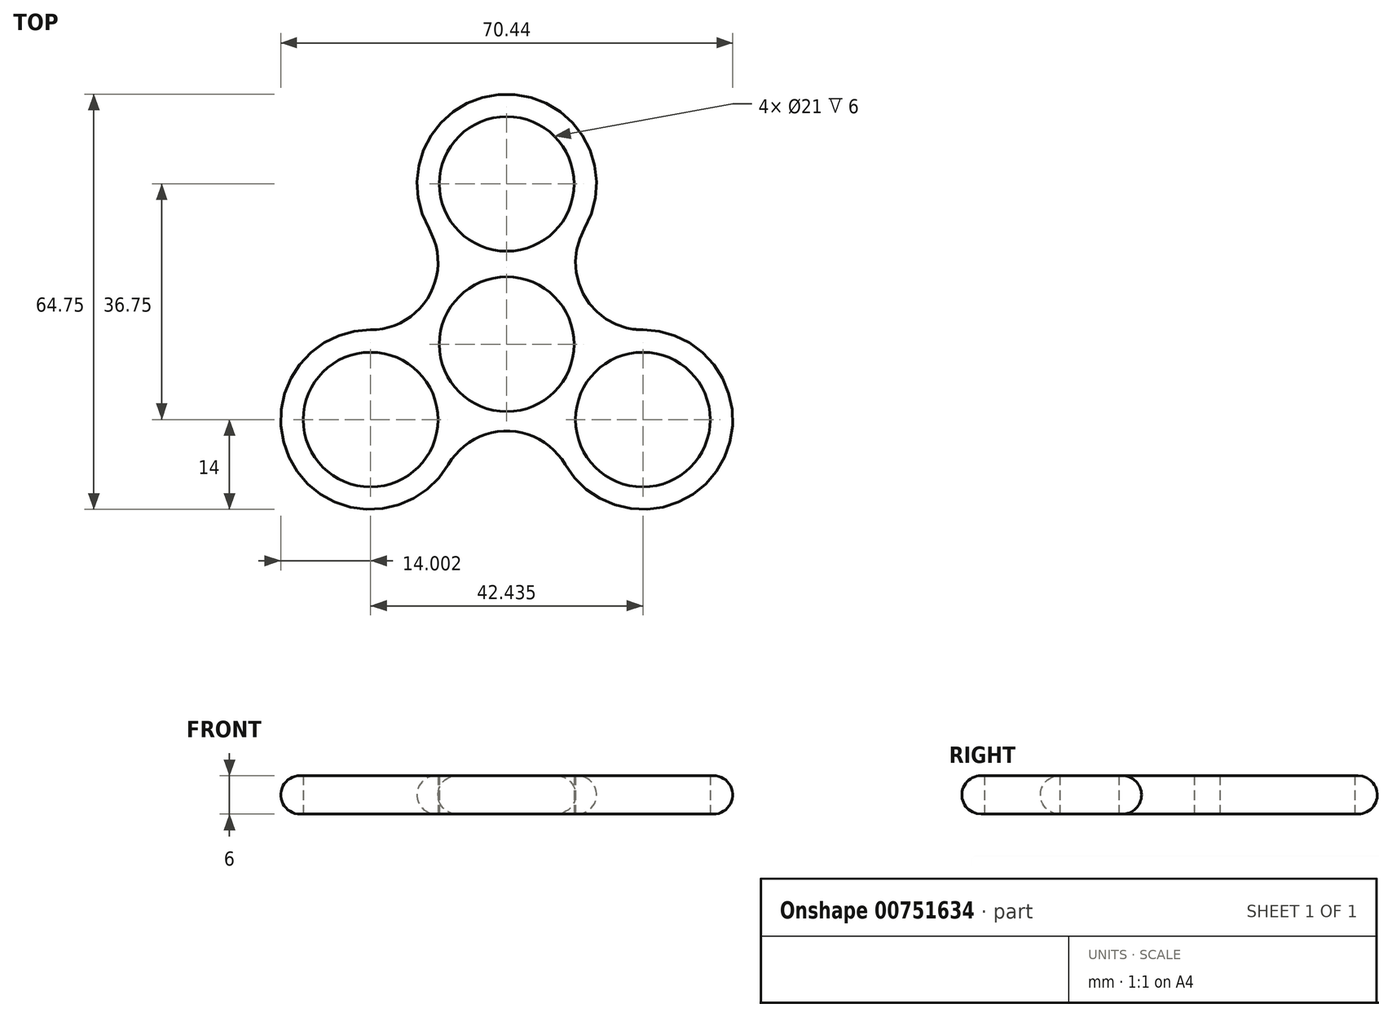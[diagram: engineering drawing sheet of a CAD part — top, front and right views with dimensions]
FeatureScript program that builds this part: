
annotation { "Feature Type Name" : "Feature", "Feature Type Description" : "" }
export const myFeature = defineFeature(function(context is Context, id is Id, definition is map)
    precondition{}
    {
        {
            var Q0;
            Q0=qCreatedBy(makeId("Top.planeOp"),FACE);
            var sketch = newSketch(context, id + "F0", { "sketchPlane" : qUnion([Q0])});
            skCircle(sketch, "E0", {"center": v(0, 0) * mm, "radius": 10.5 * mm});
            skCircle(sketch, "E1", {"center": v(0, 25) * mm, "radius": 10.5 * mm});
            skArc(sketch, "E2.1.0", {"start": v(-21.22, 2.25) * mm, "mid": v(-12.12, 7.5) * mm, "end": v(-12.12, 18) * mm});
            skCircle(sketch, "E2.2.0", {"center": v(-21.22, -11.75) * mm, "radius": 10.5 * mm});
            skPoint(sketch, "E2.center", {"position": v(0, 0.5) * mm});
            skArc(sketch, "E3", {"start": v(12.12, 18) * mm, "mid": v(0, 39) * mm, "end": v(-12.12, 18) * mm});
            skArc(sketch, "E4.1.0", {"start": v(-21.22, 2.25) * mm, "mid": v(-33.34, -18.75) * mm, "end": v(-9.1, -18.75) * mm});
            skArc(sketch, "E4.2.0", {"start": v(9.1, -18.75) * mm, "mid": v(33.34, -18.75) * mm, "end": v(21.22, 2.25) * mm});
            skArc(sketch, "E5.1.3.0", {"start": v(9.1, -18.75) * mm, "mid": v(0, -13.5) * mm, "end": v(-9.1, -18.75) * mm});
            skCircle(sketch, "E5.1.4.0", {"center": v(21.22, -11.75) * mm, "radius": 10.5 * mm});
            skArc(sketch, "E5.1.5.0", {"start": v(12.12, 18) * mm, "mid": v(12.12, 7.5) * mm, "end": v(21.22, 2.25) * mm});
            skSolve(sketch);
        }
        {
            var Q0;
            Q0=makeQuery(id+"F0.imprint","IMPRINT",FACE,{"disambiguationData":[TD([[makeQuery(id+"F0.imprint","IMPRINT",EDGE,{"derivedFrom":sQuery(id+"F0.wireOp",EDGE,"E0")}),-1.0]])]});
            extrude(context, id + "F1", {"entities" : qUnion([Q0]), "depth" : 6 * mm, "offsetDistance" : 25 * mm});
        }
        {
            var Q0;
            Q0=makeQuery(id+"F1.opExtrude","CAP_EDGE",EDGE,{"disambiguationData":[OSD([sQuery(id+"F0.wireOp",EDGE,"E5.1.3.0")])],"isStart":false});
            var Q1;
            Q1=makeQuery(id+"F1.opExtrude","CAP_EDGE",EDGE,{"disambiguationData":[OSD([sQuery(id+"F0.wireOp",EDGE,"E4.2.0")])],"isStart":false});
            var Q2;
            Q2=makeQuery(id+"F1.opExtrude","SWEPT_FACE",FACE,{"disambiguationData":[OSD([sQuery(id+"F0.wireOp",EDGE,"E4.1.0")])]});
            fillet(context, id + "F2", {"entities" : qUnion([Q0, Q1, Q2]), "radius" : 3 * mm, "tangentPropagation" : true, "allowEdgeOverflow" : false});
        }
    });
